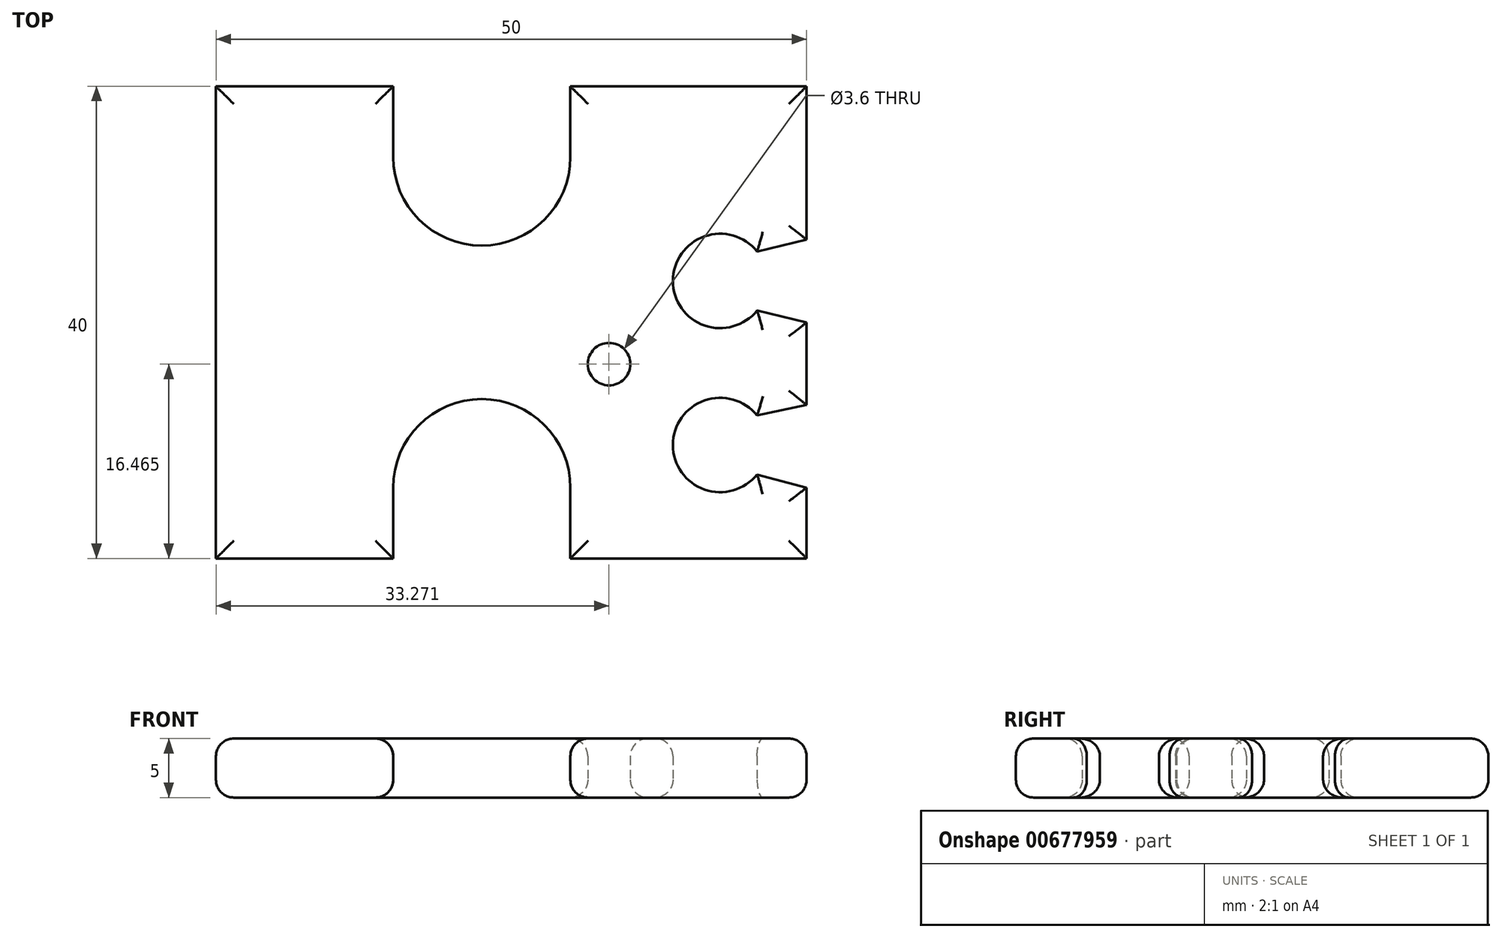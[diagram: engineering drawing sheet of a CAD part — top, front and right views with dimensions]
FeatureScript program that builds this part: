
annotation { "Feature Type Name" : "Feature", "Feature Type Description" : "" }
export const myFeature = defineFeature(function(context is Context, id is Id, definition is map)
    precondition{}
    {
        {
            var Q0;
            Q0=qCreatedBy(makeId("Top.planeOp"),FACE);
            var sketch = newSketch(context, id + "F0", { "sketchPlane" : qUnion([Q0])});
            skLineSegment(sketch, "E0", {"start": v(-61.6, 14) * mm, "end": v(-61.6, -26) * mm});
            skLineSegment(sketch, "E1", {"start": v(-61.6, -26) * mm, "end": v(-46.6, -26) * mm});
            skLineSegment(sketch, "E2", {"start": v(-46.6, -26) * mm, "end": v(-46.6, -20) * mm});
            skArc(sketch, "E3", {"start": v(-31.6, -20) * mm, "mid": v(-39.1, -12.5) * mm, "end": v(-46.6, -20) * mm});
            skLineSegment(sketch, "E4", {"start": v(-31.6, -20) * mm, "end": v(-31.6, -26) * mm});
            skLineSegment(sketch, "E5", {"start": v(-31.6, -26) * mm, "end": v(-11.6, -26) * mm});
            skLineSegment(sketch, "E6", {"start": v(-11.6, -26) * mm, "end": v(-11.6, -20) * mm});
            skLineSegment(sketch, "E7", {"start": v(-11.6, -20) * mm, "end": v(-15.8, -18.9) * mm});
            skArc(sketch, "E8", {"start": v(-15.8, -13.9) * mm, "mid": v(-22.92, -16.4) * mm, "end": v(-15.8, -18.9) * mm});
            skLineSegment(sketch, "E9", {"start": v(-15.8, -13.9) * mm, "end": v(-11.6, -13) * mm});
            skLineSegment(sketch, "E10", {"start": v(-11.6, -13) * mm, "end": v(-11.6, -6) * mm});
            skLineSegment(sketch, "E11", {"start": v(-11.6, -6) * mm, "end": v(-15.8, -5) * mm});
            skArc(sketch, "E12", {"start": v(-15.8, 0) * mm, "mid": v(-22.92, -2.5) * mm, "end": v(-15.8, -5) * mm});
            skLineSegment(sketch, "E13", {"start": v(-15.8, 0) * mm, "end": v(-11.6, 1) * mm});
            skLineSegment(sketch, "E14", {"start": v(-11.6, 1) * mm, "end": v(-11.6, 14) * mm});
            skCircle(sketch, "E15", {"center": v(-28.33, -9.54) * mm, "radius": 1.8 * mm});
            skLineSegment(sketch, "E16", {"start": v(-61.6, 14) * mm, "end": v(-46.6, 14) * mm});
            skLineSegment(sketch, "E17", {"start": v(-46.6, 14) * mm, "end": v(-46.6, 8) * mm});
            skLineSegment(sketch, "E18", {"start": v(-11.6, 14) * mm, "end": v(-31.6, 14) * mm});
            skLineSegment(sketch, "E19", {"start": v(-31.6, 14) * mm, "end": v(-31.6, 8) * mm});
            skArc(sketch, "E20", {"start": v(-46.6, 8) * mm, "mid": v(-39.1, 0.5) * mm, "end": v(-31.6, 8) * mm});
            skSolve(sketch);
        }
        {
            var Q0;
            Q0=makeQuery(id+"F0.imprint","IMPRINT",FACE,{"disambiguationData":[TD([[makeQuery(id+"F0.imprint","IMPRINT",EDGE,{"derivedFrom":sQuery(id+"F0.wireOp",EDGE,"E0")}),1.0]])]});
            extrude(context, id + "F1", {"entities" : qUnion([Q0]), "endBound" : BoundingType.SYMMETRIC, "depth" : 5 * mm, "offsetDistance" : 25 * mm});
        }
        {
            var Q0;
            Q0=makeQuery(id+"F1.opExtrude","CAP_EDGE",EDGE,{"disambiguationData":[OSD([sQuery(id+"F0.wireOp",EDGE,"E0")])],"isStart":false});
            var Q1;
            Q1=makeQuery(id+"F1.opExtrude","CAP_EDGE",EDGE,{"disambiguationData":[OSD([sQuery(id+"F0.wireOp",EDGE,"E16")])],"isStart":false});
            var Q2;
            Q2=makeQuery(id+"F1.opExtrude","CAP_EDGE",EDGE,{"disambiguationData":[OSD([sQuery(id+"F0.wireOp",EDGE,"E20")])],"isStart":false});
            var Q3;
            Q3=makeQuery(id+"F1.opExtrude","CAP_EDGE",EDGE,{"disambiguationData":[OSD([sQuery(id+"F0.wireOp",EDGE,"E18")])],"isStart":false});
            var Q4;
            Q4=makeQuery(id+"F1.opExtrude","CAP_EDGE",EDGE,{"disambiguationData":[OSD([sQuery(id+"F0.wireOp",EDGE,"E14")])],"isStart":false});
            var Q5;
            Q5=makeQuery(id+"F1.opExtrude","CAP_EDGE",EDGE,{"disambiguationData":[OSD([sQuery(id+"F0.wireOp",EDGE,"E13")])],"isStart":false});
            var Q6;
            Q6=makeQuery(id+"F1.opExtrude","CAP_EDGE",EDGE,{"disambiguationData":[OSD([sQuery(id+"F0.wireOp",EDGE,"E12")])],"isStart":false});
            var Q7;
            Q7=makeQuery(id+"F1.opExtrude","CAP_EDGE",EDGE,{"disambiguationData":[OSD([sQuery(id+"F0.wireOp",EDGE,"E11")])],"isStart":false});
            var Q8;
            Q8=makeQuery(id+"F1.opExtrude","CAP_EDGE",EDGE,{"disambiguationData":[OSD([sQuery(id+"F0.wireOp",EDGE,"E10")])],"isStart":false});
            var Q9;
            Q9=makeQuery(id+"F1.opExtrude","CAP_EDGE",EDGE,{"disambiguationData":[OSD([sQuery(id+"F0.wireOp",EDGE,"E9")])],"isStart":false});
            var Q10;
            Q10=makeQuery(id+"F1.opExtrude","CAP_EDGE",EDGE,{"disambiguationData":[OSD([sQuery(id+"F0.wireOp",EDGE,"E8")])],"isStart":false});
            var Q11;
            Q11=makeQuery(id+"F1.opExtrude","CAP_EDGE",EDGE,{"disambiguationData":[OSD([sQuery(id+"F0.wireOp",EDGE,"E7")])],"isStart":false});
            var Q12;
            Q12=makeQuery(id+"F1.opExtrude","CAP_FACE",FACE,{"disambiguationData":[OSD([sQuery(id+"F0.wireOp",EDGE,"E0"),sQuery(id+"F0.wireOp",EDGE,"E1"),sQuery(id+"F0.wireOp",EDGE,"E2"),sQuery(id+"F0.wireOp",EDGE,"E3"),sQuery(id+"F0.wireOp",EDGE,"E4"),sQuery(id+"F0.wireOp",EDGE,"E5"),sQuery(id+"F0.wireOp",EDGE,"E6"),sQuery(id+"F0.wireOp",EDGE,"E7"),sQuery(id+"F0.wireOp",EDGE,"E8"),sQuery(id+"F0.wireOp",EDGE,"E9"),sQuery(id+"F0.wireOp",EDGE,"E10"),sQuery(id+"F0.wireOp",EDGE,"E11"),sQuery(id+"F0.wireOp",EDGE,"E12"),sQuery(id+"F0.wireOp",EDGE,"E13"),sQuery(id+"F0.wireOp",EDGE,"E14"),sQuery(id+"F0.wireOp",EDGE,"E15"),sQuery(id+"F0.wireOp",EDGE,"E16"),sQuery(id+"F0.wireOp",EDGE,"E17"),sQuery(id+"F0.wireOp",EDGE,"E18"),sQuery(id+"F0.wireOp",EDGE,"E19"),sQuery(id+"F0.wireOp",EDGE,"E20")])],"isStart":false});
            fillet(context, id + "F2", {"entities" : qUnion([Q0, Q1, Q2, Q3, Q4, Q5, Q6, Q7, Q8, Q9, Q10, Q11, Q12]), "radius" : 1.5 * mm, "tangentPropagation" : true, "allowEdgeOverflow" : false});
        }
        {
            var Q0;
            Q0=makeQuery(id+"F1.opExtrude","CAP_FACE",FACE,{"disambiguationData":[OSD([sQuery(id+"F0.wireOp",EDGE,"E0"),sQuery(id+"F0.wireOp",EDGE,"E1"),sQuery(id+"F0.wireOp",EDGE,"E2"),sQuery(id+"F0.wireOp",EDGE,"E3"),sQuery(id+"F0.wireOp",EDGE,"E4"),sQuery(id+"F0.wireOp",EDGE,"E5"),sQuery(id+"F0.wireOp",EDGE,"E6"),sQuery(id+"F0.wireOp",EDGE,"E7"),sQuery(id+"F0.wireOp",EDGE,"E8"),sQuery(id+"F0.wireOp",EDGE,"E9"),sQuery(id+"F0.wireOp",EDGE,"E10"),sQuery(id+"F0.wireOp",EDGE,"E11"),sQuery(id+"F0.wireOp",EDGE,"E12"),sQuery(id+"F0.wireOp",EDGE,"E13"),sQuery(id+"F0.wireOp",EDGE,"E14"),sQuery(id+"F0.wireOp",EDGE,"E15"),sQuery(id+"F0.wireOp",EDGE,"E16"),sQuery(id+"F0.wireOp",EDGE,"E17"),sQuery(id+"F0.wireOp",EDGE,"E18"),sQuery(id+"F0.wireOp",EDGE,"E19"),sQuery(id+"F0.wireOp",EDGE,"E20")])],"isStart":true});
            fillet(context, id + "F3", {"entities" : qUnion([Q0]), "radius" : 1.5 * mm, "tangentPropagation" : true, "allowEdgeOverflow" : false});
        }
    });
